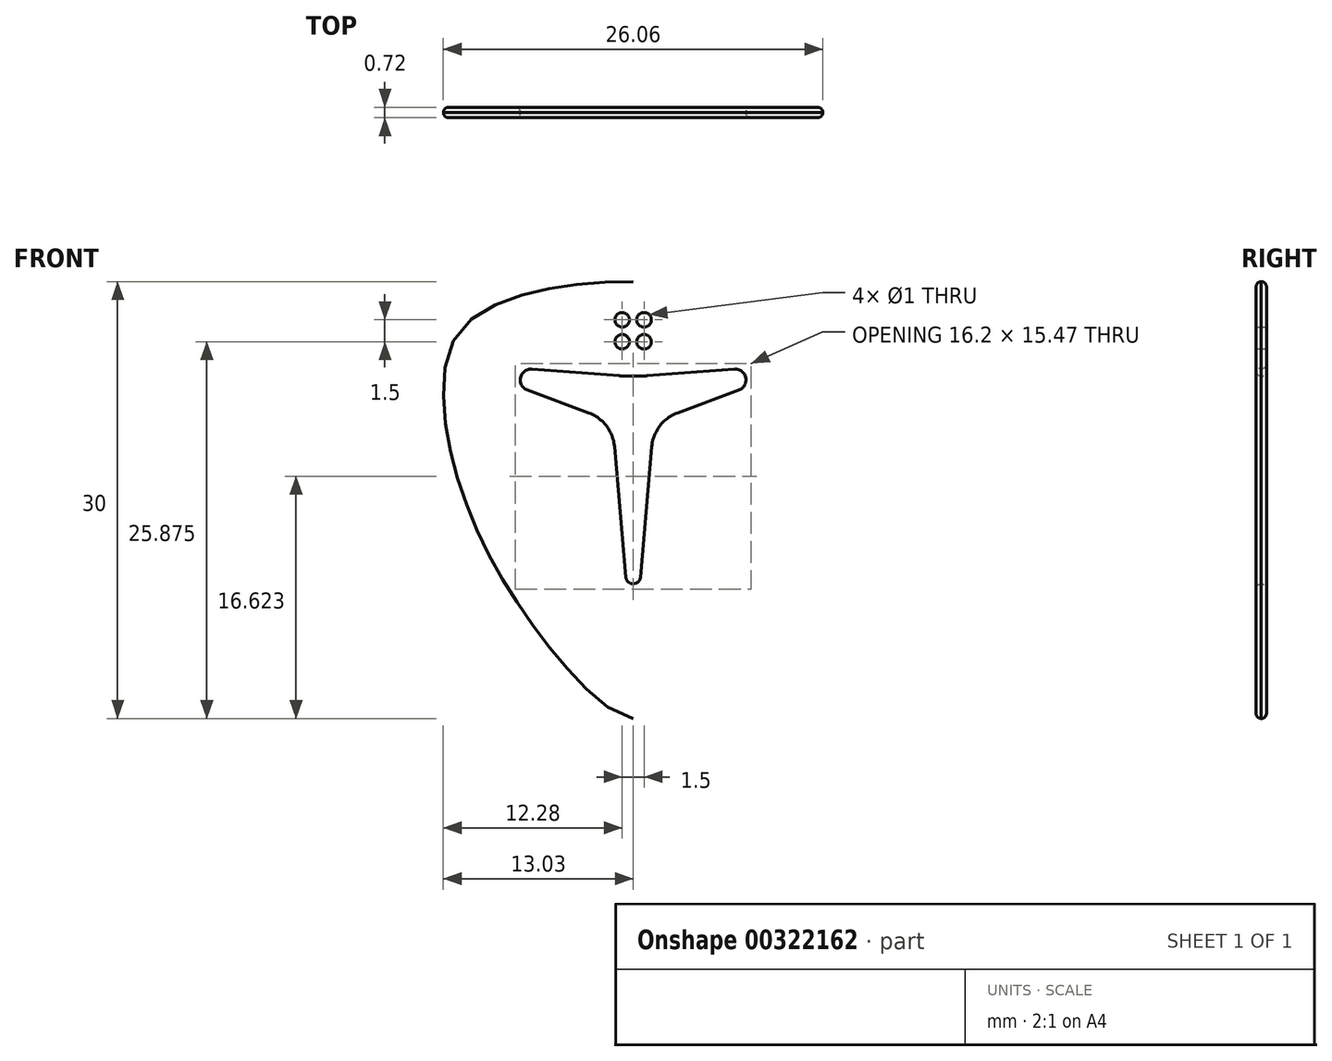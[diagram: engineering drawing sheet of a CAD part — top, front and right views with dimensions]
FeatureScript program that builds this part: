
annotation { "Feature Type Name" : "Feature", "Feature Type Description" : "" }
export const myFeature = defineFeature(function(context is Context, id is Id, definition is map)
    precondition{}
    {
        {
            var Q0;
            Q0=qCreatedBy(makeId("Front.planeOp"),FACE);
            var sketch = newSketch(context, id + "F0", { "sketchPlane" : qUnion([Q0])});
            skLineSegment(sketch, "E0", {"start": v(0, 0) * mm, "end": v(0, 6.75) * mm, "construction": true});
            skLineSegment(sketch, "E1", {"start": v(0, 0) * mm, "end": v(0, -23.25) * mm, "construction": true});
            skLineSegment(sketch, "E2", {"start": v(0, 0) * mm, "end": v(13, 0) * mm, "construction": true});
            skFitSpline(sketch, "E3", {"points": [v(0, -23.25) * mm, v(9.5, -12.75) * mm, v(13, 0) * mm, v(11, 4.25) * mm, v(0, 6.75) * mm], "startDerivative": vector(20.6, 0) * mm, "endDerivative": vector(-57.72, 0) * mm});
            skFitSpline(sketch, "E4.MirrorCS", {"points": [v(0, -23.25) * mm, v(-9.5, -12.75) * mm, v(-13, 0) * mm, v(-11, 4.25) * mm, v(0, 6.75) * mm], "startDerivative": vector(-20.6, 0) * mm, "endDerivative": vector(57.72, 0) * mm});
            skArc(sketch, "E5", {"start": v(7.26, -0.7) * mm, "mid": v(7.73, 0.16) * mm, "end": v(6.94, 0.75) * mm});
            skLineSegment(sketch, "E6", {"start": v(7.26, -0.7) * mm, "end": v(3.04, -2.27) * mm});
            skArc(sketch, "E7", {"start": v(3.04, -2.27) * mm, "mid": v(1.83, -3.17) * mm, "end": v(1.28, -4.58) * mm});
            skLineSegment(sketch, "E8", {"start": v(0.5, -13.54) * mm, "end": v(1.28, -4.58) * mm});
            skArc(sketch, "E9", {"start": v(0, -14) * mm, "mid": v(0.34, -13.87) * mm, "end": v(0.5, -13.54) * mm});
            skArc(sketch, "E10.MirrorCS", {"start": v(0, -14) * mm, "mid": v(-0.34, -13.87) * mm, "end": v(-0.5, -13.54) * mm});
            skLineSegment(sketch, "E11.MirrorCS", {"start": v(-0.5, -13.54) * mm, "end": v(-1.28, -4.58) * mm});
            skArc(sketch, "E12.MirrorCS", {"start": v(-3.04, -2.27) * mm, "mid": v(-1.83, -3.17) * mm, "end": v(-1.28, -4.58) * mm});
            skLineSegment(sketch, "E13.MirrorCS", {"start": v(-7.26, -0.7) * mm, "end": v(-3.04, -2.27) * mm});
            skArc(sketch, "E14.MirrorCS", {"start": v(-7.26, -0.7) * mm, "mid": v(-7.73, 0.16) * mm, "end": v(-6.94, 0.75) * mm});
            skLineSegment(sketch, "E15", {"start": v(6.94, 0.75) * mm, "end": v(0.96, 0.29) * mm});
            skArc(sketch, "E16", {"start": v(0, 0.25) * mm, "mid": v(0.48, 0.26) * mm, "end": v(0.96, 0.29) * mm});
            skArc(sketch, "E17.MirrorCS", {"start": v(0, 0.25) * mm, "mid": v(-0.48, 0.26) * mm, "end": v(-0.96, 0.29) * mm});
            skLineSegment(sketch, "E18.MirrorCS", {"start": v(-6.94, 0.75) * mm, "end": v(-0.96, 0.29) * mm});
            skLineSegment(sketch, "E19.bottom", {"start": v(-0.75, 4.12) * mm, "end": v(0.75, 4.12) * mm, "construction": true});
            skLineSegment(sketch, "E19.top", {"start": v(-0.75, 2.63) * mm, "end": v(0.75, 2.63) * mm, "construction": true});
            skLineSegment(sketch, "E19.left", {"start": v(-0.75, 4.12) * mm, "end": v(-0.75, 2.63) * mm, "construction": true});
            skLineSegment(sketch, "E19.right", {"start": v(0.75, 4.12) * mm, "end": v(0.75, 2.63) * mm, "construction": true});
            skPoint(sketch, "E20", {"position": v(0, 4.12) * mm});
            skPoint(sketch, "E21", {"position": v(-0.75, 3.38) * mm});
            skPoint(sketch, "E22", {"position": v(0, 3.38) * mm});
            skCircle(sketch, "E23", {"center": v(0.75, 4.12) * mm, "radius": 0.5 * mm});
            skCircle(sketch, "E24", {"center": v(0.75, 2.63) * mm, "radius": 0.5 * mm});
            skCircle(sketch, "E25.MirrorC", {"center": v(-0.75, 4.12) * mm, "radius": 0.5 * mm});
            skCircle(sketch, "E26.MirrorC", {"center": v(-0.75, 2.63) * mm, "radius": 0.5 * mm});
            skSolve(sketch);
        }
        {
            var Q0;
            Q0=qSketchRegion(id+"F0",true);
            extrude(context, id + "F1", {"entities" : qUnion([Q0]), "depth" : 0.72 * mm});
        }
        {
            var Q0;
            Q0=makeQuery(id+"F1.opExtrude","CAP_EDGE",EDGE,{"disambiguationData":[OSD([sQuery(id+"F0.wireOp",EDGE,"E5")])],"isStart":false});
            var Q1;
            Q1=makeQuery(id+"F1.opExtrude","CAP_EDGE",EDGE,{"disambiguationData":[OSD([sQuery(id+"F0.wireOp",EDGE,"E7")])],"isStart":true});
            var Q2;
            Q2=makeQuery(id+"F1.opExtrude","CAP_EDGE",EDGE,{"disambiguationData":[OSD([sQuery(id+"F0.wireOp",EDGE,"E9"),sQuery(id+"F0.wireOp",EDGE,"E10.MirrorCS")])],"isStart":false});
            var Q3;
            Q3=makeQuery(id+"F1.opExtrude","CAP_EDGE",EDGE,{"disambiguationData":[OSD([sQuery(id+"F0.wireOp",EDGE,"E14.MirrorCS")])],"isStart":false});
            var Q4;
            Q4=makeQuery(id+"F1.opExtrude","CAP_EDGE",EDGE,{"disambiguationData":[OSD([sQuery(id+"F0.wireOp",EDGE,"E5")])],"isStart":true});
            var Q5;
            Q5=makeQuery(id+"F1.opExtrude","CAP_EDGE",EDGE,{"disambiguationData":[OSD([sQuery(id+"F0.wireOp",EDGE,"E12.MirrorCS")])],"isStart":false});
            var Q6;
            Q6=makeQuery(id+"F1.opExtrude","CAP_EDGE",EDGE,{"disambiguationData":[OSD([sQuery(id+"F0.wireOp",EDGE,"E7")])],"isStart":false});
            var Q7;
            Q7=makeQuery(id+"F1.opExtrude","CAP_EDGE",EDGE,{"disambiguationData":[OSD([sQuery(id+"F0.wireOp",EDGE,"cP70XH3B-hxny-nh1n-TbyW-52Zl4TOD4HrO"),sQuery(id+"F0.wireOp",EDGE,"9cf6c757-e815-40dd-95a7-672993b90d513.MirrorCS")])],"isStart":true});
            var Q8;
            Q8=makeQuery(id+"F1.opExtrude","CAP_EDGE",EDGE,{"disambiguationData":[OSD([sQuery(id+"F0.wireOp",EDGE,"E13.MirrorCS")])],"isStart":false});
            var Q9;
            Q9=makeQuery(id+"F1.opExtrude","CAP_EDGE",EDGE,{"disambiguationData":[OSD([sQuery(id+"F0.wireOp",EDGE,"E12.MirrorCS")])],"isStart":true});
            var Q10;
            Q10=makeQuery(id+"F1.opExtrude","CAP_EDGE",EDGE,{"disambiguationData":[OSD([sQuery(id+"F0.wireOp",EDGE,"cP70XH3B-hxny-nh1n-TbyW-52Zl4TOD4HrO"),sQuery(id+"F0.wireOp",EDGE,"9cf6c757-e815-40dd-95a7-672993b90d513.MirrorCS")])],"isStart":false});
            var Q11;
            Q11=makeQuery(id+"F1.opExtrude","CAP_EDGE",EDGE,{"disambiguationData":[OSD([sQuery(id+"F0.wireOp",EDGE,"E9"),sQuery(id+"F0.wireOp",EDGE,"E10.MirrorCS")])],"isStart":true});
            var Q12;
            Q12=makeQuery(id+"F1.opExtrude","SWEPT_EDGE",EDGE,{"disambiguationData":[OSD([sQuery(id+"F0.wireOp",EDGE,"9cf6c757-e815-40dd-95a7-672993b90d513.MirrorCS"),sQuery(id+"F0.wireOp",EDGE,"E14.MirrorCS")])]});
            var Q13;
            Q13=makeQuery(id+"F1.opExtrude","CAP_EDGE",EDGE,{"disambiguationData":[OSD([sQuery(id+"F0.wireOp",EDGE,"E8")])],"isStart":true});
            var Q14;
            Q14=makeQuery(id+"F1.opExtrude","CAP_EDGE",EDGE,{"disambiguationData":[OSD([sQuery(id+"F0.wireOp",EDGE,"E11.MirrorCS")])],"isStart":false});
            var Q15;
            Q15=makeQuery(id+"F1.opExtrude","SWEPT_EDGE",EDGE,{"disambiguationData":[OSD([sQuery(id+"F0.wireOp",EDGE,"E6"),sQuery(id+"F0.wireOp",EDGE,"E7")])]});
            var Q16;
            Q16=makeQuery(id+"F1.opExtrude","SWEPT_EDGE",EDGE,{"disambiguationData":[OSD([sQuery(id+"F0.wireOp",EDGE,"E8"),sQuery(id+"F0.wireOp",EDGE,"E9")])]});
            var Q17;
            Q17=makeQuery(id+"F1.opExtrude","SWEPT_EDGE",EDGE,{"disambiguationData":[OSD([sQuery(id+"F0.wireOp",EDGE,"E13.MirrorCS"),sQuery(id+"F0.wireOp",EDGE,"E14.MirrorCS")])]});
            var Q18;
            Q18=makeQuery(id+"F1.opExtrude","SWEPT_EDGE",EDGE,{"disambiguationData":[OSD([sQuery(id+"F0.wireOp",EDGE,"E10.MirrorCS"),sQuery(id+"F0.wireOp",EDGE,"E11.MirrorCS")])]});
            var Q19;
            Q19=makeQuery(id+"F1.opExtrude","SWEPT_EDGE",EDGE,{"disambiguationData":[OSD([sQuery(id+"F0.wireOp",EDGE,"E11.MirrorCS"),sQuery(id+"F0.wireOp",EDGE,"E12.MirrorCS")])]});
            var Q20;
            Q20=makeQuery(id+"F1.opExtrude","SWEPT_EDGE",EDGE,{"disambiguationData":[OSD([sQuery(id+"F0.wireOp",EDGE,"E5"),sQuery(id+"F0.wireOp",EDGE,"E6")])]});
            var Q21;
            Q21=makeQuery(id+"F1.opExtrude","CAP_EDGE",EDGE,{"disambiguationData":[OSD([sQuery(id+"F0.wireOp",EDGE,"E14.MirrorCS")])],"isStart":true});
            var Q22;
            Q22=makeQuery(id+"F1.opExtrude","SWEPT_EDGE",EDGE,{"disambiguationData":[OSD([sQuery(id+"F0.wireOp",EDGE,"E12.MirrorCS"),sQuery(id+"F0.wireOp",EDGE,"E13.MirrorCS")])]});
            var Q23;
            Q23=makeQuery(id+"F1.opExtrude","CAP_EDGE",EDGE,{"disambiguationData":[OSD([sQuery(id+"F0.wireOp",EDGE,"E8")])],"isStart":false});
            var Q24;
            Q24=makeQuery(id+"F1.opExtrude","SWEPT_EDGE",EDGE,{"disambiguationData":[OSD([sQuery(id+"F0.wireOp",EDGE,"cP70XH3B-hxny-nh1n-TbyW-52Zl4TOD4HrO"),sQuery(id+"F0.wireOp",EDGE,"E5")])]});
            var Q25;
            Q25=makeQuery(id+"F1.opExtrude","CAP_EDGE",EDGE,{"disambiguationData":[OSD([sQuery(id+"F0.wireOp",EDGE,"E6")])],"isStart":false});
            var Q26;
            Q26=makeQuery(id+"F1.opExtrude","CAP_EDGE",EDGE,{"disambiguationData":[OSD([sQuery(id+"F0.wireOp",EDGE,"E11.MirrorCS")])],"isStart":true});
            var Q27;
            Q27=makeQuery(id+"F1.opExtrude","SWEPT_EDGE",EDGE,{"disambiguationData":[OSD([sQuery(id+"F0.wireOp",EDGE,"E7"),sQuery(id+"F0.wireOp",EDGE,"E8")])]});
            var Q28;
            Q28=makeQuery(id+"F1.opExtrude","CAP_EDGE",EDGE,{"disambiguationData":[OSD([sQuery(id+"F0.wireOp",EDGE,"E6")])],"isStart":true});
            var Q29;
            Q29=makeQuery(id+"F1.opExtrude","CAP_EDGE",EDGE,{"disambiguationData":[OSD([sQuery(id+"F0.wireOp",EDGE,"E13.MirrorCS")])],"isStart":true});
            var Q30;
            Q30=makeQuery(id+"F1.opExtrude","CAP_EDGE",EDGE,{"disambiguationData":[OSD([sQuery(id+"F0.wireOp",EDGE,"E18.MirrorCS")])],"isStart":false});
            var Q31;
            Q31=makeQuery(id+"F1.opExtrude","CAP_EDGE",EDGE,{"disambiguationData":[OSD([sQuery(id+"F0.wireOp",EDGE,"E18.MirrorCS")])],"isStart":true});
            var Q32;
            Q32=makeQuery(id+"F1.opExtrude","CAP_EDGE",EDGE,{"disambiguationData":[OSD([sQuery(id+"F0.wireOp",EDGE,"E16"),sQuery(id+"F0.wireOp",EDGE,"E17.MirrorCS")])],"isStart":false});
            var Q33;
            Q33=makeQuery(id+"F1.opExtrude","CAP_EDGE",EDGE,{"disambiguationData":[OSD([sQuery(id+"F0.wireOp",EDGE,"E16"),sQuery(id+"F0.wireOp",EDGE,"E17.MirrorCS")])],"isStart":true});
            var Q34;
            Q34=makeQuery(id+"F1.opExtrude","CAP_EDGE",EDGE,{"disambiguationData":[OSD([sQuery(id+"F0.wireOp",EDGE,"E15")])],"isStart":false});
            var Q35;
            Q35=makeQuery(id+"F1.opExtrude","CAP_EDGE",EDGE,{"disambiguationData":[OSD([sQuery(id+"F0.wireOp",EDGE,"E15")])],"isStart":true});
            fillet(context, id + "F2", {"entities" : qUnion([Q0, Q1, Q2, Q3, Q4, Q5, Q6, Q7, Q8, Q9, Q10, Q11, Q12, Q13, Q14, Q15, Q16, Q17, Q18, Q19, Q20, Q21, Q22, Q23, Q24, Q25, Q26, Q27, Q28, Q29, Q30, Q31, Q32, Q33, Q34, Q35]), "radius" : (0.72 / 2) * mm, "tangentPropagation" : true, "allowEdgeOverflow" : false});
        }
        {
            var Q0;
            Q0=makeQuery(id+"F1.opExtrude","CAP_EDGE",EDGE,{"disambiguationData":[OSD([sQuery(id+"F0.wireOp",EDGE,"E4.MirrorCS")])],"isStart":false});
            var Q1;
            Q1=makeQuery(id+"F1.opExtrude","CAP_EDGE",EDGE,{"disambiguationData":[OSD([sQuery(id+"F0.wireOp",EDGE,"E3")])],"isStart":false});
            var Q2;
            Q2=makeQuery(id+"F1.opExtrude","CAP_EDGE",EDGE,{"disambiguationData":[OSD([sQuery(id+"F0.wireOp",EDGE,"E4.MirrorCS")])],"isStart":true});
            var Q3;
            Q3=makeQuery(id+"F1.opExtrude","CAP_EDGE",EDGE,{"disambiguationData":[OSD([sQuery(id+"F0.wireOp",EDGE,"E3")])],"isStart":true});
            fillet(context, id + "F3", {"entities" : qUnion([Q0, Q1, Q2, Q3]), "radius" : 0.72 / 2 * mm, "tangentPropagation" : true, "allowEdgeOverflow" : false});
        }
    });
